# Revit family: STH9300_27_30
name_source: partatom
category: Luminárias
units: mm (PartAtom-declared; Revit-internal decimal feet)

## family parameters
Com base no plano de trabalho = Não
Compartilhado = Não
Corte com vazios quando carregada = Não
Cota do conector redondo = Utilizar diâmetro
Fonte luminosa = Sim
Manter orientação da anotação = Não
Ponto de cálculo do ambiente = Não
Sempre na vertical = Sim
Tipo de parte = Normal

## types (2) — shared parameters
Altura = 0.1 m
Dimerização = Não dimerizável
Diâmetro = 0.04 m
Estrutura = Al - Branco
Fabricante = Stella
Filtro de cor = 16777215
Fluxo Luminoso = 250 lm
Grau de proteção (IP) = IP20
IRC (Índice de reprodução de cores) = >80
Modelo = Vela Fosca
Potência = 3 W
Tensão Elétrica = 100V-240V
Troca de temperatura da cor de lâmpada com esmaecimento = <Nenhum>
URL = https://stella.com.br
Ângulo de Abertura = 230º
Ângulo de inclinação = 90.00°
zero-valued in all types: Elevação padrão

## per-type parameters (varying)
| type | Arquivo de rede fotométrica | Luminoso | Referência | Temperatura da cor (K) |
| STH9300/27 - BIVOLT - 2700K - 250lm - 230° | STELLA - STH9300-27 - VELA FOSCA 3W.ies | Luminoso - 2700K | STH9300/27 - BIVOLT | 2700 K |
| STH9300/30 - BIVOLT - 3000K - 250lm - 230° | STELLA - STH9300-30 - VELA FOSCA 3W.ies | Luminoso - 3000K | STH9300/30 - BIVOLT | 3000 K |
